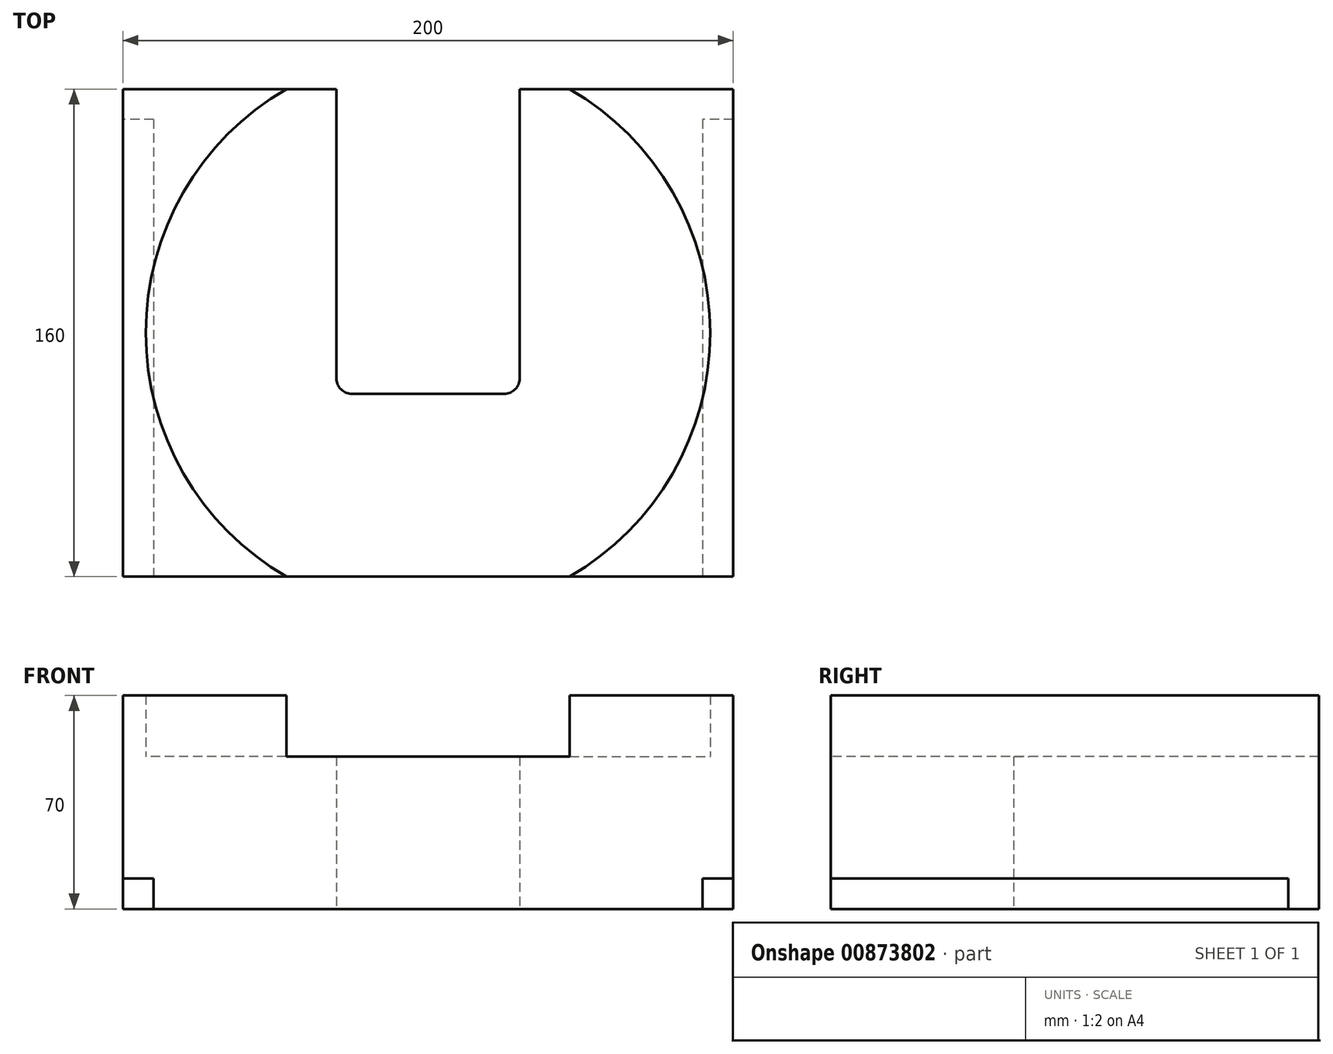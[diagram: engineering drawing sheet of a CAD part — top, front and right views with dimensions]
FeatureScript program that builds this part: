
annotation { "Feature Type Name" : "Feature", "Feature Type Description" : "" }
export const myFeature = defineFeature(function(context is Context, id is Id, definition is map)
    precondition{}
    {
        {
            var Q0;
            Q0=qCreatedBy(makeId("Top.planeOp"),FACE);
            var sketch = newSketch(context, id + "F0", { "sketchPlane" : qUnion([Q0])});
            skLineSegment(sketch, "E0.bottom", {"start": v(100, -80) * mm, "end": v(-100, -80) * mm});
            skLineSegment(sketch, "E0.top", {"start": v(100, 80) * mm, "end": v(-100, 80) * mm});
            skLineSegment(sketch, "E0.left", {"start": v(100, -80) * mm, "end": v(100, 80) * mm});
            skLineSegment(sketch, "E0.right", {"start": v(-100, -80) * mm, "end": v(-100, 80) * mm});
            skPoint(sketch, "E0.middle", {"position": v(0, 0) * mm});
            skSolve(sketch);
        }
        {
            var Q0;
            Q0=qSketchRegion(id+"F0",true);
            extrude(context, id + "F1", {"entities" : qUnion([Q0]), "depth" : 50 * mm, "offsetDistance" : 25 * mm});
        }
        {
            var Q0;
            Q0=makeQuery(id+"F1.opExtrude","CAP_FACE",FACE,{"disambiguationData":[OSD([sQuery(id+"F0.wireOp",EDGE,"E0.bottom"),sQuery(id+"F0.wireOp",EDGE,"E0.top"),sQuery(id+"F0.wireOp",EDGE,"E0.left"),sQuery(id+"F0.wireOp",EDGE,"E0.right")])],"isStart":false});
            var sketch = newSketch(context, id + "F2", { "sketchPlane" : qUnion([Q0])});
            skCircle(sketch, "E1", {"center": v(0, 0) * mm, "radius": 92.5 * mm});
            skCircle(sketch, "E2", {"center": v(0, 0) * mm, "radius": 75 * mm});
            skSolve(sketch);
        }
        {
            var Q0;
            {var subQ5=makeQuery(id+"F1.opExtrude","CAP_EDGE",EDGE,{"disambiguationData":[OSD([sQuery(id+"F0.wireOp",EDGE,"E0.left")])],"isStart":false});Q0=makeQuery(id+"F2.imprint","IMPRINT",FACE,{"disambiguationData":[TD([[makeQuery(id+"F2.imprint","IMPRINT",EDGE,{"derivedFrom":subQ5}),1.0]])]});}
            var Q1;
            {var subQ5=makeQuery(id+"F1.opExtrude","CAP_EDGE",EDGE,{"disambiguationData":[OSD([sQuery(id+"F0.wireOp",EDGE,"E0.right")])],"isStart":false});Q1=makeQuery(id+"F2.imprint","IMPRINT",FACE,{"disambiguationData":[TD([[makeQuery(id+"F2.imprint","IMPRINT",EDGE,{"derivedFrom":subQ5}),-1.0]])]});}
            extrude(context, id + "F3", {"entities" : qUnion([Q0, Q1]), "operationType" : NewBodyOperationType.ADD, "depth" : 20 * mm, "offsetDistance" : 25 * mm});
        }
        {
            var Q0;
            Q0=makeQuery(id+"F1.opExtrude","CAP_FACE",FACE,{"disambiguationData":[OSD([sQuery(id+"F0.wireOp",EDGE,"E0.bottom"),sQuery(id+"F0.wireOp",EDGE,"E0.top"),sQuery(id+"F0.wireOp",EDGE,"E0.left"),sQuery(id+"F0.wireOp",EDGE,"E0.right")])],"isStart":false});
            var sketch = newSketch(context, id + "F4", { "sketchPlane" : qUnion([Q0])});
            skCircle(sketch, "E3", {"center": v(0, 0) * mm, "radius": 30 * mm});
            skSolve(sketch);
        }
        {
            var Q0;
            Q0=qCreatedBy(makeId("Front.planeOp"),FACE);
            var sketch = newSketch(context, id + "F5", { "sketchPlane" : qUnion([Q0])});
            skLineSegment(sketch, "E4.bottom", {"start": v(30, 60) * mm, "end": v(-30, 60) * mm});
            skLineSegment(sketch, "E4.top", {"start": v(30, -60) * mm, "end": v(-30, -60) * mm});
            skLineSegment(sketch, "E4.left", {"start": v(30, 60) * mm, "end": v(30, -60) * mm});
            skLineSegment(sketch, "E4.right", {"start": v(-30, 60) * mm, "end": v(-30, -60) * mm});
            skPoint(sketch, "E4.middle", {"position": v(0, 0) * mm});
            skSolve(sketch);
        }
        {
            var Q0;
            {var subQ0=sQuery(id+"F5.wireOp",EDGE,"E4.left");var subQ1=sQuery(id+"F0.wireOp",EDGE,"E0.bottom");var subQ2=makeQuery(id+"F1.opExtrude","CAP_EDGE",EDGE,{"disambiguationData":[OSD([subQ1])],"isStart":false});var subQ3=makeQuery(id+"F5.imprint","INTERSECT",VERTEX,{"derivedFrom":[subQ2,subQ0]});Q0=makeQuery(id+"F5.imprint","IMPRINT",FACE,{"disambiguationData":[TD([[makeQuery(id+"F5.imprint","IMPRINT",EDGE,{"disambiguationData":[TD([[subQ3,-1.0]])],"derivedFrom":subQ0}),-1.0]])]});}
            var Q1;
            {var subQ0=sQuery(id+"F5.wireOp",EDGE,"E4.bottom");Q1=makeQuery(id+"F5.imprint","IMPRINT",FACE,{"disambiguationData":[TD([[makeQuery(id+"F5.imprint","IMPRINT",EDGE,{"derivedFrom":subQ0}),1.0]])]});}
            var Q2;
            {var subQ0=sQuery(id+"F5.wireOp",EDGE,"E4.top");Q2=makeQuery(id+"F5.imprint","IMPRINT",FACE,{"disambiguationData":[TD([[makeQuery(id+"F5.imprint","IMPRINT",EDGE,{"derivedFrom":subQ0}),-1.0]])]});}
            extrude(context, id + "F6", {"entities" : qUnion([Q0, Q1, Q2]), "operationType" : NewBodyOperationType.REMOVE, "oppositeDirection" : true, "depth" : 90 * mm, "offsetDistance" : 25 * mm, "hasSecondDirection" : true, "secondDirectionOppositeDirection" : false, "secondDirectionDepth" : 20 * mm});
        }
        {
            var Q0;
            Q0=makeQuery(id+"F3.opExtrude","CAP_FACE",FACE,{"disambiguationData":[OSD([sQuery(id+"F0.wireOp",EDGE,"E0.bottom"),sQuery(id+"F0.wireOp",EDGE,"E0.top"),sQuery(id+"F0.wireOp",EDGE,"E0.left"),sQuery(id+"F0.wireOp",EDGE,"E0.right"),sQuery(id+"F2.wireOp",EDGE,"E1")])],"isStart":false});
            var sketch = newSketch(context, id + "F7", { "sketchPlane" : qUnion([Q0])});
            skLineSegment(sketch, "E5.bottom", {"start": v(85, -65) * mm, "end": v(-85, -65) * mm});
            skLineSegment(sketch, "E5.top", {"start": v(85, 65) * mm, "end": v(-85, 65) * mm});
            skLineSegment(sketch, "E5.left", {"start": v(85, -65) * mm, "end": v(85, 65) * mm});
            skLineSegment(sketch, "E5.right", {"start": v(-85, -65) * mm, "end": v(-85, 65) * mm});
            skPoint(sketch, "E5.middle", {"position": v(0, 0) * mm});
            skSolve(sketch);
        }
        {
            var Q0;
            Q0=qCreatedBy(makeId("Front.planeOp"),FACE);
            var sketch = newSketch(context, id + "F8", { "sketchPlane" : qUnion([Q0])});
            skLineSegment(sketch, "E6.bottom", {"start": v(30, 40) * mm, "end": v(-30, 40) * mm});
            skLineSegment(sketch, "E6.top", {"start": v(30, -40) * mm, "end": v(-30, -40) * mm});
            skLineSegment(sketch, "E6.left", {"start": v(30, 40) * mm, "end": v(30, -40) * mm});
            skLineSegment(sketch, "E6.right", {"start": v(-30, 40) * mm, "end": v(-30, -40) * mm});
            skPoint(sketch, "E6.middle", {"position": v(0, 0) * mm});
            skSolve(sketch);
        }
        {
            var Q0;
            {var subQ0=sQuery(id+"F0.wireOp",EDGE,"E0.bottom");var subQ1=makeQuery(id+"F1.opExtrude","CAP_EDGE",EDGE,{"disambiguationData":[OSD([subQ0])],"isStart":false});Q0=makeQuery(id+"F3.boolean.opBoolean","MERGE",FACE,{"derivedFrom":[makeQuery(id+"F1.opExtrude","SWEPT_FACE",FACE,{"disambiguationData":[OSD([subQ0])]}),makeQuery(id+"F3.opExtrude","SWEPT_FACE",FACE,{"disambiguationData":[OSD([subQ0]),TDD([makeQuery(id+"F2.imprint","IMPRINT",EDGE,{"disambiguationData":[TD([[makeQuery(id+"F2.imprint","INTERSECT",VERTEX,{"derivedFrom":[subQ1,makeQuery(id+"F1.opExtrude","CAP_EDGE",EDGE,{"disambiguationData":[OSD([sQuery(id+"F0.wireOp",EDGE,"E0.left")])],"isStart":false})]}),-1.0]])],"derivedFrom":subQ1})])]}),makeQuery(id+"F3.opExtrude","SWEPT_FACE",FACE,{"disambiguationData":[OSD([subQ0]),TDD([makeQuery(id+"F2.imprint","IMPRINT",EDGE,{"disambiguationData":[TD([[makeQuery(id+"F2.imprint","INTERSECT",VERTEX,{"derivedFrom":[subQ1,makeQuery(id+"F1.opExtrude","CAP_EDGE",EDGE,{"disambiguationData":[OSD([sQuery(id+"F0.wireOp",EDGE,"E0.right")])],"isStart":false})]}),1.0]])],"derivedFrom":subQ1})])]})]});}
            var sketch = newSketch(context, id + "F9", { "sketchPlane" : qUnion([Q0])});
            skLineSegment(sketch, "E7.bottom", {"start": v(-90, 0) * mm, "end": v(100, 0) * mm});
            skLineSegment(sketch, "E7.top", {"start": v(-100, 10) * mm, "end": v(-90, 10) * mm});
            skLineSegment(sketch, "E7.left", {"start": v(-100, 0) * mm, "end": v(-100, 10) * mm});
            skLineSegment(sketch, "E7.right", {"start": v(-90, 0) * mm, "end": v(-90, 10) * mm});
            skLineSegment(sketch, "E8.bottom", {"start": v(90, 0) * mm, "end": v(-100, 0) * mm});
            skLineSegment(sketch, "E8.top", {"start": v(100, 10) * mm, "end": v(90, 10) * mm});
            skLineSegment(sketch, "E8.left", {"start": v(100, 0) * mm, "end": v(100, 10) * mm});
            skLineSegment(sketch, "E8.right", {"start": v(90, 0) * mm, "end": v(90, 10) * mm});
            skSolve(sketch);
        }
        {
            var Q0;
            Q0=makeQuery(id+"F9.imprint","IMPRINT",FACE,{"disambiguationData":[TD([[makeQuery(id+"F9.imprint","IMPRINT",EDGE,{"derivedFrom":sQuery(id+"F9.wireOp",EDGE,"E7.bottom")}),1.0]])]});
            var Q1;
            Q1=makeQuery(id+"F9.imprint","IMPRINT",FACE,{"disambiguationData":[TD([[makeQuery(id+"F9.imprint","IMPRINT",EDGE,{"derivedFrom":sQuery(id+"F9.wireOp",EDGE,"E8.bottom")}),-1.0]])]});
            var Q2;
            Q2=makeQuery(id+"F9.imprint","IMPRINT",FACE,{"disambiguationData":[TD([[makeQuery(id+"F9.imprint","IMPRINT",EDGE,{"derivedFrom":sQuery(id+"F9.wireOp",EDGE,"E8.bottom")}),1.0]])]});
            var Q3;
            Q3=makeQuery(id+"F9.imprint","IMPRINT",FACE,{"disambiguationData":[TD([[makeQuery(id+"F9.imprint","IMPRINT",EDGE,{"derivedFrom":sQuery(id+"F9.wireOp",EDGE,"E7.bottom")}),-1.0]])]});
            extrude(context, id + "F10", {"entities" : qUnion([Q0, Q1, Q2, Q3]), "operationType" : NewBodyOperationType.REMOVE, "oppositeDirection" : true, "depth" : 150 * mm, "offsetDistance" : 25 * mm});
        }
        {
            var Q0;
            Q0=makeQuery(id+"F6.boolean.opBoolean","COPY",EDGE,{"derivedFrom":makeQuery(id+"F6.opExtrude","CAP_EDGE",EDGE,{"disambiguationData":[OSD([sQuery(id+"F5.wireOp",EDGE,"E4.right")])],"isStart":true})});
            var Q1;
            Q1=makeQuery(id+"F6.boolean.opBoolean","COPY",EDGE,{"derivedFrom":makeQuery(id+"F6.opExtrude","CAP_EDGE",EDGE,{"disambiguationData":[OSD([sQuery(id+"F5.wireOp",EDGE,"E4.left")])],"isStart":true})});
            fillet(context, id + "F11", {"entities" : qUnion([Q0, Q1]), "tangentPropagation" : true, "radius" : 5 * mm, "defaultsChanged" : false, "vertexSettings" : [], "allowEdgeOverflow" : false});
        }
    });
